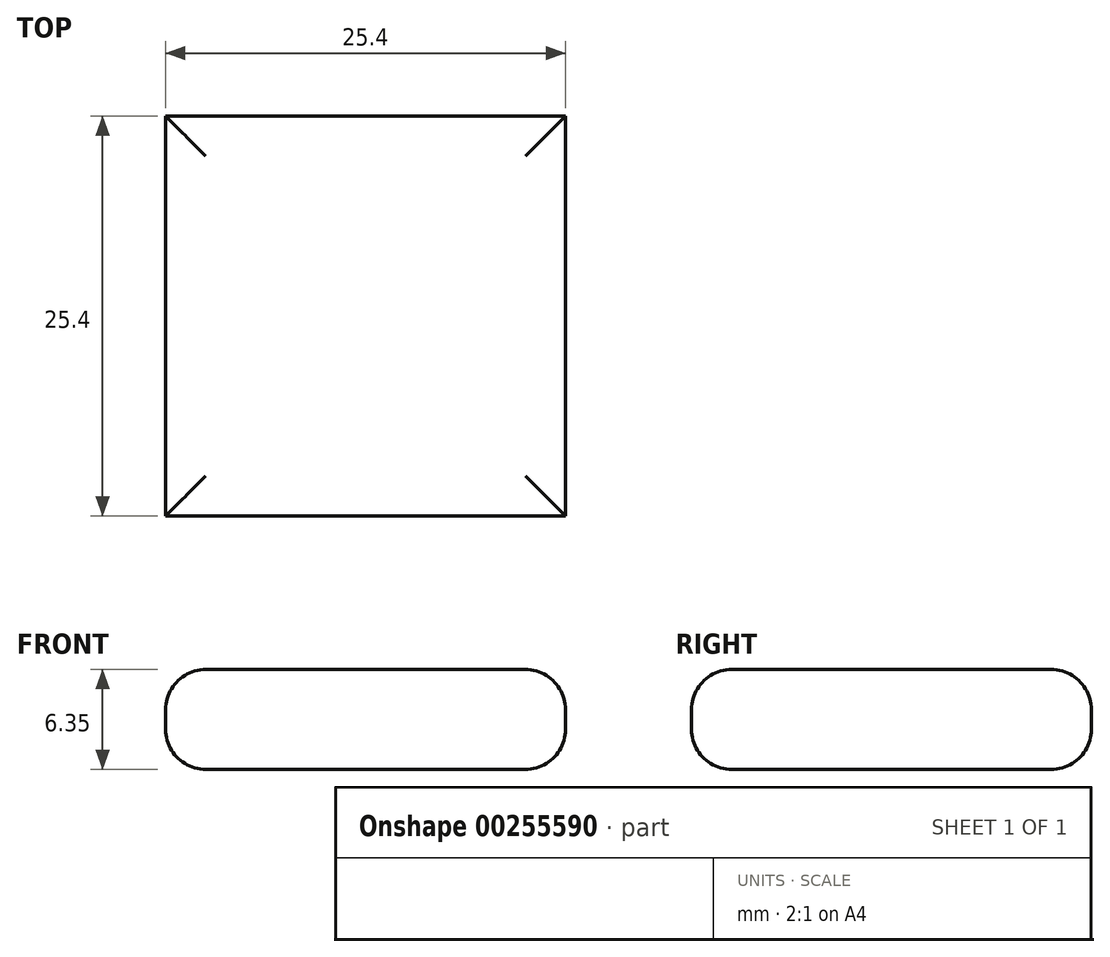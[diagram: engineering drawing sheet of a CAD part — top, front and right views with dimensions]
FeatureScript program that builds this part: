
annotation { "Feature Type Name" : "Feature", "Feature Type Description" : "" }
export const myFeature = defineFeature(function(context is Context, id is Id, definition is map)
    precondition{}
    {
        {
            var Q0;
            Q0=qCreatedBy(makeId("Top.planeOp"),FACE);
            var sketch = newSketch(context, id + "F0", { "sketchPlane" : qUnion([Q0])});
            skLineSegment(sketch, "E0.bottom", {"start": v(0, 0) * mm, "end": v(-25.4, 0) * mm});
            skLineSegment(sketch, "E0.top", {"start": v(0, 25.4) * mm, "end": v(-25.4, 25.4) * mm});
            skLineSegment(sketch, "E0.left", {"start": v(0, 0) * mm, "end": v(0, 25.4) * mm});
            skLineSegment(sketch, "E0.right", {"start": v(-25.4, 0) * mm, "end": v(-25.4, 25.4) * mm});
            skSolve(sketch);
        }
        {
            var Q0;
            Q0=qCreatedBy(makeId("Right.planeOp"),FACE);
            var sketch = newSketch(context, id + "F1", { "sketchPlane" : qUnion([Q0])});
            skSolve(sketch);
        }
        {
            var Q0;
            Q0 = qSketchRegion(id + "F1", true);
            var Q1;
            Q1=makeQuery(id+"F0.imprint","IMPRINT",FACE,{"disambiguationData":[TD([[makeQuery(id+"F0.imprint","IMPRINT",EDGE,{"derivedFrom":sQuery(id+"F0.wireOp",EDGE,"E0.bottom")}),-1.0]])]});
            extrude(context, id + "F2", {"entities" : qUnion([Q0, Q1]), "depth" : 6.35 * mm});
        }
        {
            var Q0;
            Q0=makeQuery(id+"F2.opExtrude","CAP_FACE",FACE,{"disambiguationData":[OSD([sQuery(id+"F0.wireOp",EDGE,"E0.bottom"),sQuery(id+"F0.wireOp",EDGE,"E0.top"),sQuery(id+"F0.wireOp",EDGE,"E0.left"),sQuery(id+"F0.wireOp",EDGE,"E0.right")])],"isStart":false});
            var Q1;
            Q1=makeQuery(id+"F2.opExtrude","CAP_FACE",FACE,{"disambiguationData":[OSD([sQuery(id+"F0.wireOp",EDGE,"E0.bottom"),sQuery(id+"F0.wireOp",EDGE,"E0.top"),sQuery(id+"F0.wireOp",EDGE,"E0.left"),sQuery(id+"F0.wireOp",EDGE,"E0.right")])],"isStart":true});
            fillet(context, id + "F3", {"entities" : qUnion([Q0, Q1]), "radius" : 2.54 * mm, "tangentPropagation" : true, "allowEdgeOverflow" : false});
        }
    });
